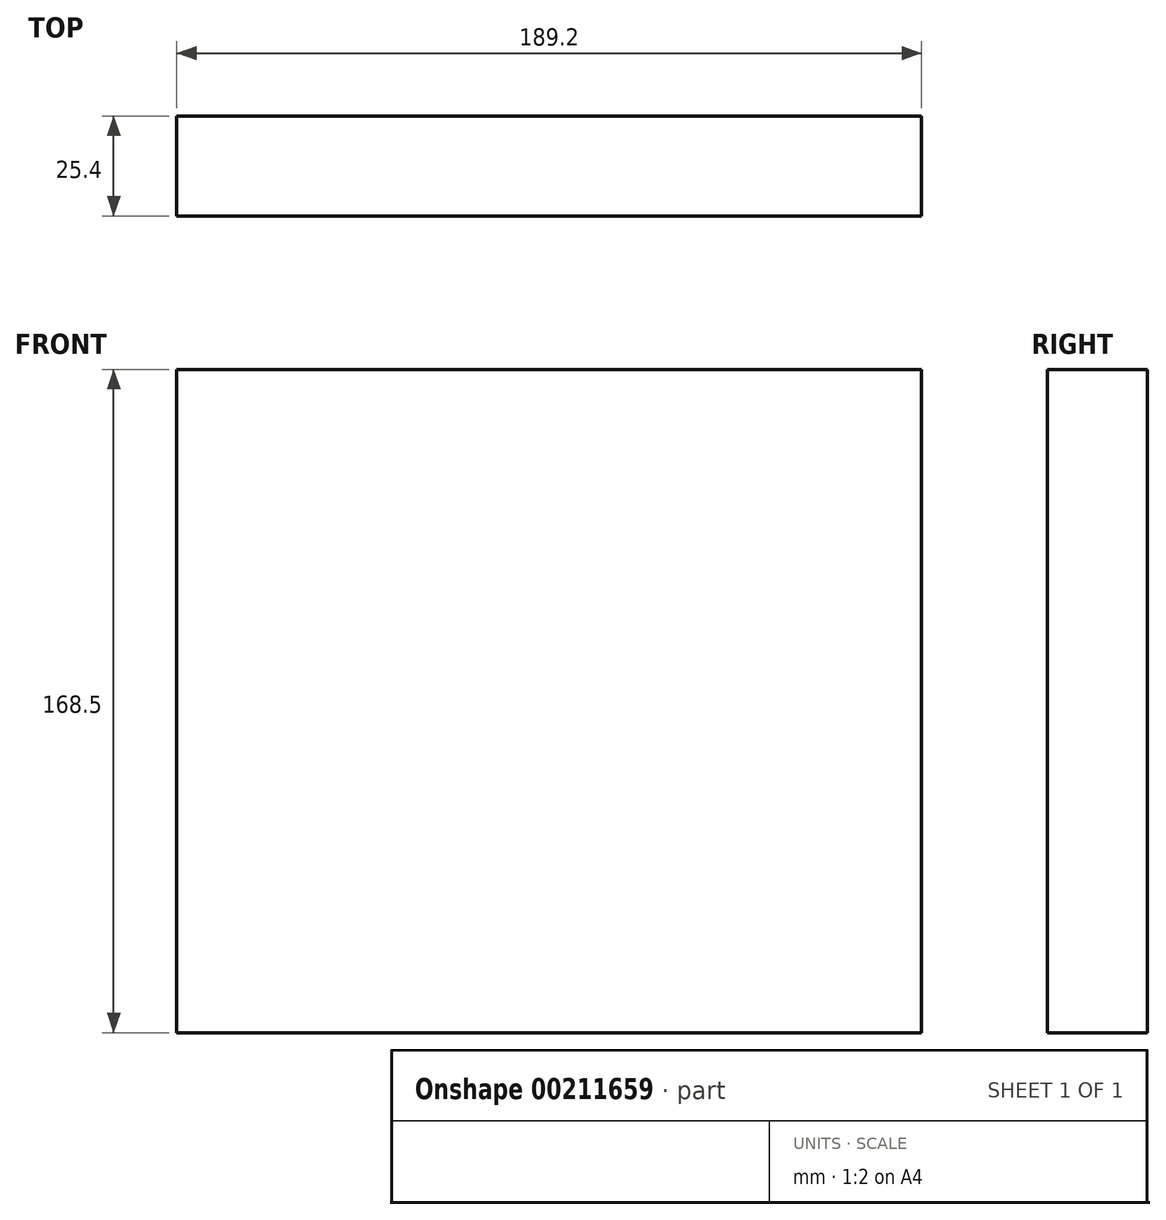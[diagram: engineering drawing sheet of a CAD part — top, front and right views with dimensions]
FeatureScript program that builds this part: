
annotation { "Feature Type Name" : "Feature", "Feature Type Description" : "" }
export const myFeature = defineFeature(function(context is Context, id is Id, definition is map)
    precondition{}
    {
        {
            var Q0;
            Q0=qCreatedBy(makeId("Front.planeOp"),FACE);
            var sketch = newSketch(context, id + "F0", { "sketchPlane" : qUnion([Q0])});
            skLineSegment(sketch, "E0.bottom", {"start": v(94.6, -84.25) * mm, "end": v(-94.6, -84.25) * mm});
            skLineSegment(sketch, "E0.top", {"start": v(94.6, 84.25) * mm, "end": v(-94.6, 84.25) * mm});
            skLineSegment(sketch, "E0.left", {"start": v(94.6, -84.25) * mm, "end": v(94.6, 84.25) * mm});
            skLineSegment(sketch, "E0.right", {"start": v(-94.6, -84.25) * mm, "end": v(-94.6, 84.25) * mm});
            skPoint(sketch, "E0.middle", {"position": v(0, 0) * mm});
            skSolve(sketch);
        }
        {
            var Q0;
            Q0=makeQuery(id+"F0.imprint","IMPRINT",FACE,{"disambiguationData":[TD([[makeQuery(id+"F0.imprint","IMPRINT",EDGE,{"derivedFrom":sQuery(id+"F0.wireOp",EDGE,"E0.bottom")}),-1.0]])]});
            extrude(context, id + "F1", {"entities" : qUnion([Q0]), "depth" : 25.4 * mm});
        }
    });
